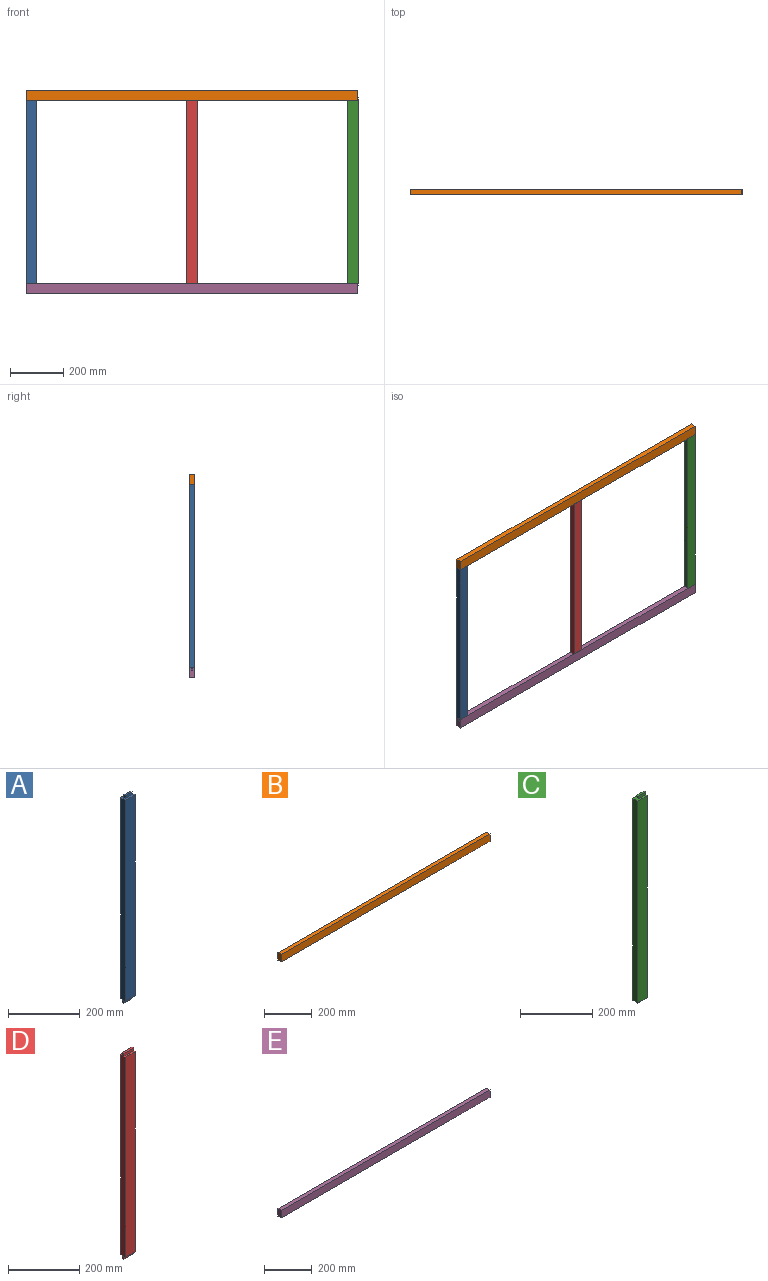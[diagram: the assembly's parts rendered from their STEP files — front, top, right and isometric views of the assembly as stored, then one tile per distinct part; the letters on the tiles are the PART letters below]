
ASSEMBLY  parts=5 mates=4
PART A: 15 faces, bbox 38.1x19.1x704.9 mm
  f0: plane 38.1x19.05mm, normal (0,0,1), area 564.5mm2, adj f1,f2,f3,f4,f6,f7,f8,f9
  f1: plane 695.33x19.05mm, normal (-1,0,0), area 13125mm2, adj f0,f2,f4,f5,f12,f13,f14
  f2: plane 685.8x38.1mm, normal (0,-1,0), area 26129mm2, adj f0,f1,f3,f5
  f3: plane 685.8x19.05mm, normal (1,0,0), area 13064.5mm2, adj f0,f2,f4,f5
  f4: plane 685.8x38.1mm, normal (0,1,0), area 26129mm2, adj f0,f1,f3,f5
  f5: plane 38.1x19.05mm, normal (0,0,-1), area 544.4mm2, adj f1,f2,f3,f4,f11,f12,f13
  f6: plane 25.4x9.53mm, normal (0,-1,0), area 241.9mm2, adj f0,f7,f9,f10
  f7: plane 9.53x6.35mm, normal (1,0,0), area 60.5mm2, adj f0,f6,f8,f10
  f8: plane 25.4x9.53mm, normal (0,1,0), area 241.9mm2, adj f0,f7,f9,f10
  f9: plane 9.53x6.35mm, normal (-1,0,0), area 60.5mm2, adj f0,f6,f8,f10
  f10: plane 25.4x6.35mm, normal (0,0,1), area 161.3mm2, adj f6,f7,f8,f9
  f11: plane 9.53x6.35mm, normal (1,0,0), area 60.5mm2, adj f5,f12,f13,f14
  f12: plane 28.58x9.53mm, normal (0,-1,0), area 272.2mm2, adj f1,f5,f11,f14
  f13: plane 28.58x9.53mm, normal (0,1,0), area 272.2mm2, adj f1,f5,f11,f14
  f14: plane 28.58x6.35mm, normal (0,0,-1), area 181.5mm2, adj f1,f11,f12,f13
PART B: 6 faces, bbox 1241.4x19.1x38.1 mm
  f0: plane 1241.43x38.1mm, normal (0,-1,0), area 47298.3mm2, adj f1,f3,f4,f5
  f1: plane 1241.43x19.05mm, normal (0,0,-1), area 23649.1mm2, adj f0,f2,f4,f5
  f2: plane 1241.43x38.1mm, normal (0,1,0), area 47298.3mm2, adj f1,f3,f4,f5
  f3: plane 1241.43x19.05mm, normal (0,0,1), area 23649.1mm2, adj f0,f2,f4,f5
  f4: plane 38.1x19.05mm, normal (1,0,0), area 725.8mm2, adj f0,f1,f2,f3
  f5: plane 38.1x19.05mm, normal (-1,0,0), area 725.8mm2, adj f0,f1,f2,f3
PART C: 14 faces, bbox 38.1x19.1x702.3 mm
  f0: plane 38.1x19.05mm, normal (0,0,1), area 544.4mm2, adj f1,f2,f3,f4,f6,f7,f8
  f1: plane 702.31x19.05mm, normal (1,0,0), area 13169.3mm2, adj f0,f2,f4,f5,f7,f8,f9,f11
  f2: plane 685.8x38.1mm, normal (0,1,0), area 26129mm2, adj f0,f1,f3,f5
  f3: plane 685.8x19.05mm, normal (-1,0,0), area 13064.5mm2, adj f0,f2,f4,f5
  f4: plane 685.8x38.1mm, normal (0,-1,0), area 26129mm2, adj f0,f1,f3,f5
  f5: plane 38.1x19.05mm, normal (0,0,-1), area 544.4mm2, adj f1,f2,f3,f4,f10,f11,f12
  f6: plane 9.53x6.35mm, normal (-1,0,0), area 60.5mm2, adj f0,f7,f8,f9
  f7: plane 28.58x9.53mm, normal (0,-1,0), area 272.2mm2, adj f0,f1,f6,f9
  f8: plane 28.58x9.53mm, normal (0,1,0), area 272.2mm2, adj f0,f1,f6,f9
  f9: plane 28.58x6.35mm, normal (0,0,1), area 181.5mm2, adj f1,f6,f7,f8
  f10: plane 6.99x6.35mm, normal (-1,0,0), area 44.4mm2, adj f5,f11,f12,f13
  f11: plane 28.58x6.99mm, normal (0,1,0), area 199.6mm2, adj f1,f5,f10,f13
  f12: plane 28.58x6.99mm, normal (0,-1,0), area 199.6mm2, adj f1,f5,f10,f13
  f13: plane 28.58x6.35mm, normal (0,0,-1), area 181.5mm2, adj f1,f10,f11,f12
PART D: 14 faces, bbox 38.1x19.1x704.9 mm
  f0: plane 38.1x6.35mm, normal (0,0,-1), area 241.9mm2, adj f2,f4,f5,f12
  f1: plane 38.1x6.35mm, normal (0,0,1), area 241.9mm2, adj f2,f4,f5,f8
  f2: plane 704.85x19.05mm, normal (-1,0,0), area 13185.5mm2, adj f0,f1,f3,f5,f6,f7,f8,f9
  f3: plane 685.8x38.1mm, normal (0,-1,0), area 26129mm2, adj f2,f4,f6,f7
  f4: plane 704.85x19.05mm, normal (1,0,0), area 13185.5mm2, adj f0,f1,f3,f5,f6,f7,f8,f9
  f5: plane 685.8x38.1mm, normal (0,1,0), area 26129mm2, adj f0,f1,f2,f4
  f6: plane 38.1x6.35mm, normal (0,0,1), area 241.9mm2, adj f2,f3,f4,f9
  f7: plane 38.1x6.35mm, normal (0,0,-1), area 241.9mm2, adj f2,f3,f4,f11
  f8: plane 38.1x9.53mm, normal (0,1,0), area 362.9mm2, adj f1,f2,f4,f10
  f9: plane 38.1x9.53mm, normal (0,-1,0), area 362.9mm2, adj f2,f4,f6,f10
  f10: plane 38.1x6.35mm, normal (0,0,1), area 241.9mm2, adj f2,f4,f8,f9
  f11: plane 38.1x9.53mm, normal (0,-1,0), area 362.9mm2, adj f2,f4,f7,f13
  f12: plane 38.1x9.53mm, normal (0,1,0), area 362.9mm2, adj f0,f2,f4,f13
  f13: plane 38.1x6.35mm, normal (0,0,-1), area 241.9mm2, adj f2,f4,f11,f12
PART E: 6 faces, bbox 1241.4x19.1x38.1 mm
  f0: plane 1241.43x38.1mm, normal (0,1,0), area 47298.3mm2, adj f1,f3,f4,f5
  f1: plane 1241.43x19.05mm, normal (0,0,1), area 23649.1mm2, adj f0,f2,f4,f5
  f2: plane 1241.43x38.1mm, normal (0,-1,0), area 47298.3mm2, adj f1,f3,f4,f5
  f3: plane 1241.43x19.05mm, normal (0,0,-1), area 23649.1mm2, adj f0,f2,f4,f5
  f4: plane 38.1x19.05mm, normal (1,0,0), area 725.8mm2, adj f0,f1,f2,f3
  f5: plane 38.1x19.05mm, normal (-1,0,0), area 725.8mm2, adj f0,f1,f2,f3
PLACE A t=(-88.76,144.46,-759.95)mm fixed
PLACE B t=(-88.76,144.46,-74.15)mm
PLACE C t=(1152.67,163.51,-759.95)mm
PLACE D t=(512.9,144.46,-759.95)mm
PLACE E t=(-88.76,163.51,-836.15)mm
MATE fastened C.f4 <-> B.f0  axis (0,-1,0) through (1152.67,144.46,-74.15)mm
MATE fastened E.f2 <-> C.f4  axis (0,-1,0) through (1152.67,144.46,-759.95)mm
MATE fastened A.f2 <-> B.f0  axis (0,-1,0) through (-88.76,144.46,-74.15)mm
MATE fastened D.f3 <-> B.f0  axis (0,-1,0) through (531.95,144.46,-74.15)mm
